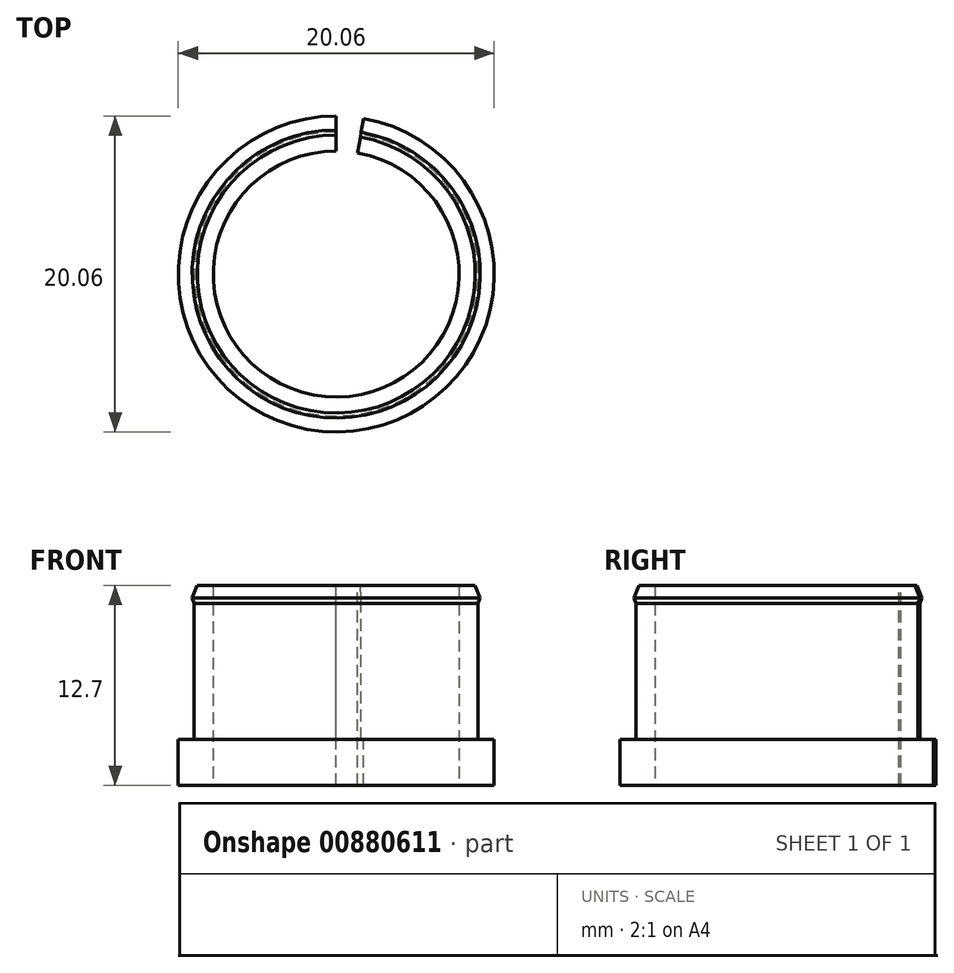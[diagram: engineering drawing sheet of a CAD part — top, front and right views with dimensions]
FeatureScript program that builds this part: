
annotation { "Feature Type Name" : "Feature", "Feature Type Description" : "" }
export const myFeature = defineFeature(function(context is Context, id is Id, definition is map)
    precondition{}
    {
        {
            var Q0;
            Q0=qCreatedBy(makeId("Right.planeOp"),FACE);
            var sketch = newSketch(context, id + "F0", { "sketchPlane" : qUnion([Q0])});
            skLineSegment(sketch, "E0", {"start": v(7.81, 0) * mm, "end": v(10.03, 0) * mm});
            skLineSegment(sketch, "E1", {"start": v(10.03, 0) * mm, "end": v(10.03, 2.92) * mm});
            skLineSegment(sketch, "E2", {"start": v(10.03, 2.92) * mm, "end": v(9.02, 2.92) * mm});
            skLineSegment(sketch, "E3", {"start": v(9.02, 2.92) * mm, "end": v(9.02, 11.56) * mm});
            skLineSegment(sketch, "E4", {"start": v(9.02, 11.56) * mm, "end": v(9.15, 11.92) * mm});
            skLineSegment(sketch, "E5", {"start": v(7.81, 0) * mm, "end": v(7.81, 12.7) * mm});
            skLineSegment(sketch, "E6", {"start": v(8.83, 12.7) * mm, "end": v(7.81, 12.7) * mm});
            skLineSegment(sketch, "E7", {"start": v(9.15, 11.92) * mm, "end": v(8.83, 12.7) * mm});
            skSolve(sketch);
        }
        {
            var Q0;
            Q0=qCreatedBy(makeId("Right.planeOp"),FACE);
            var sketch = newSketch(context, id + "F1", { "sketchPlane" : qUnion([Q0])});
            skLineSegment(sketch, "E8", {"start": v(0, 0) * mm, "end": v(0, 30.13) * mm});
            skSolve(sketch);
        }
        {
            var Q0;
            Q0=makeQuery(id+"F0.imprint","IMPRINT",FACE,{"disambiguationData":[TD([[makeQuery(id+"F0.imprint","IMPRINT",EDGE,{"derivedFrom":sQuery(id+"F0.wireOp",EDGE,"E0")}),1.0]])]});
            var Q1;
            Q1=sQuery(id+"F1.wireOp",EDGE,"E8");
            revolve(context, id + "F2", {"surfaceOperationType" : NewSurfaceOperationType.NEW, "entities" : qUnion([Q0]), "axis" : qUnion([Q1]), "revolveType" : RevolveType.ONE_DIRECTION, "angle" : 350 * degree});
        }
    });
